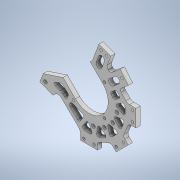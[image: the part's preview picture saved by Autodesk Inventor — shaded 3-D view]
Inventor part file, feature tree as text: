
AUTODESK INVENTOR PART (.ipt)
format: ipt  version: 2020 (Build 240168000, 168)  size: 1,079,296 bytes
history: native  units: mm
features: reference x29, sketch x22, extrude x18, projected_geometry x15, fillet x14, other x11, thicken_offset x5, hole x4, pattern_circular x3
ambient origin geometry x8: Origin, YZ Plane, XZ Plane, XY Plane, X Axis, Y Axis, Z Axis, Center Point
bodies: Solid1 (feature_tree)
feature tree (121):
  extrude  "Extrusion1"  Depth=45.0mm
  extrude  "Extrusion2"  Depth=5.0mm TaperAngle=0.0deg
  hole  "Hole1"  [1 undecoded]
  extrude  "Extrusion3"  Depth=10.0mm TaperAngle=0.0deg
  extrude  "Extrusion4"  Depth=10.0mm TaperAngle=0.0deg
  extrude  "Extrusion5"  Depth=3.0mm
  extrude  "Extrusion6"  Depth=3.0mm
  extrude  "Extrusion7"  Depth=3.0mm
  hole  "Hole2"  [1 undecoded]
  extrude  "Extrusion8"  Depth=7.0mm
  extrude  "Extrusion9"  Depth=10.0mm TaperAngle=0.0deg
  extrude  "Extrusion10"  Depth=10.0mm
  hole  "Hole3"  [1 undecoded]
  extrude  "Extrusion11"  Depth=10.0mm TaperAngle=0.0deg
  pattern_circular  "Circular Pattern1"  Count=6  [1 undecoded]
  pattern_circular  "Circular Pattern2"  Count=3  [1 undecoded]
  fillet  "Fillet3"  Radius=30.0mm
  pattern_circular  "Circular Pattern3"  Count=5  [1 undecoded]
  extrude  "Extrusion12"  Depth=2.0mm
  fillet  "Fillet5"  Radius=4.15mm
  extrude  "Extrusion14"  Depth=2.0mm
  extrude  "Extrusion15"  Depth=2.0mm
  thicken_offset  "Thicken1"
  fillet  "Fillet7"  Radius=10.0mm
  fillet  "Fillet8"  Radius=4.0mm
  extrude  "Extrusion16"  Depth=10.0mm TaperAngle=0.0deg
  hole  "Hole4"  [1 undecoded]
  fillet  "Fillet9"  Radius=1.0mm
  fillet  "Fillet10"  Radius=1.0mm
  fillet  "Fillet11"  Radius=5.0mm
  fillet  "Fillet12"  Radius=8.0mm
  extrude  "Extrusion17"  Depth=5.0mm TaperAngle=0.0deg
  fillet  "Fillet16"  Radius=6.0mm
  thicken_offset  "Thicken2"
  thicken_offset  "Thicken3"
  fillet  "Fillet17"  Radius=3.0mm
  fillet  "Fillet18"  Radius=4.0mm
  fillet  "Fillet19"  Radius=8.0mm
  fillet  "Fillet20"  Radius=5.0mm
  extrude  "Extrusion18"  Depth=2.0mm
  thicken_offset  "Thicken4"
  thicken_offset  "Thicken5"
  extrude  "Extrusion19"  Depth=2.0mm
  fillet  "Fillet21"  Radius=1.0mm
  sketch  "Sketch1"  dims[d0=109.0mm d1=45.0mm]
  reference  "Reference1"
  reference  "Reference2"
  reference  "Reference3"
  reference  "Reference4"
  sketch  "Sketch2"  dims[d2=106.0mm d3=5.0mm d4=0.0mm]
  reference  "Reference5"
  reference  "Reference6"
  reference  "Reference7"
  sketch  "Sketch3"  dims[d5=10.0mm d6=0.0mm]
  reference  "Reference8"
  reference  "Reference9"
  reference  "Reference10"
  reference  "Reference11"
  reference  "Reference12"
  reference  "Reference13"
  sketch  "Sketch4"  dims[d7=4.15mm d8=6.0mm d9=4.0mm d10=2.0mm d11=90.0deg d12=7.0mm d13=0.0mm d14=45.0mm]
  reference  "Reference14"
  sketch  "Sketch5"  dims[d15=10.0mm d16=0.0mm d17=10.0mm d18=0.0mm]
  projected_geometry  "Projected Loop1"
  reference  "Reference15"
  reference  "Reference16"
  reference  "Reference17"
  reference  "Reference18"
  sketch  "Sketch6"  dims[d19=10.0mm d20=0.0mm d21=10.0mm d22=0.0mm]
  projected_geometry  "Projected Loop2"
  sketch  "Sketch7"  dims[d24=3.0mm d25=3.0mm]
  projected_geometry  "Projected Loop3"
  sketch  "Sketch8"  dims[d26=3.0mm d27=3.0mm]
  sketch  "Sketch9"  dims[d28=3.0mm d29=3.0mm]
  projected_geometry  "Projected Loop4"
  reference  "Reference19"
  reference  "Reference20"
  sketch  "Sketch10"  dims[d30=10.0mm d31=0.0mm]
  projected_geometry  "Projected Loop5"
  sketch  "Sketch11"  dims[d32=3.0mm d33=6.0mm d34=4.0mm d35=2.0mm d36=90.0deg d37=7.0mm d38=0.0mm d39=7.0mm]
  projected_geometry  "Projected Loop6"
  sketch  "Sketch12"  dims[d40=7.0mm d41=7.0mm]
  projected_geometry  "Projected Loop7"
  sketch  "Sketch13"  dims[d42=7.0mm d43=10.0mm d44=0.0mm]
  reference  "Reference21"
  reference  "Reference22"
  reference  "Reference23"
  sketch  "Sketch14"  dims[d45=10.0mm d46=10.0mm]
  sketch  "Sketch15"  dims[d47=10.0mm d48=0.0mm d49=10.0mm]
  projected_geometry  "Projected Loop8"
  sketch  "Sketch17"  dims[d50=10.0mm d51=10.0mm d52=0.0mm]
  projected_geometry  "Projected Loop10"
  sketch  "Sketch18"  dims[d54=3.0mm d55=6.0mm d56=4.0mm d57=2.0mm d58=90.0deg d59=7.0mm d60=0.0mm d61=60.0mm]
  reference  "Reference24"
  reference  "Reference25"
  projected_geometry  "Projected Loop11"
  sketch  "Sketch19"  dims[d62=85.0mm]
  reference  "Reference26"
  projected_geometry  "Projected Loop12"
  sketch  "Sketch20"  dims[d63=30.0deg]
  projected_geometry  "Projected Loop13"
  reference  "Reference27"
  reference  "Reference28"
  reference  "Reference29"
  sketch  "Sketch21"  dims[d64=30.0deg]
  projected_geometry  "Projected Loop14"
  sketch  "Sketch22"  dims[d65=10.0mm d66=0.0mm d67=30.0mm d68=8.37758mm d70=30.0mm d71=8.37758mm]
  projected_geometry  "Projected Loop15"
  sketch  "Sketch23"  dims[d73=2.0mm d74=50.0mm d75=16.755161mm d77=4.15mm d78=4.15mm d79=4.15mm d80=4.15mm d81=10.0mm d82=0.0mm d89=4.0mm d91=10.0mm d92=0.0mm d93=5.0mm d94=0.0mm d95=1.0mm d96=1.0mm d97=5.0mm d98=8.0mm d99=5.0mm d100=0.0mm d101=3.0mm d102=6.0mm d103=4.0mm d104=2.0mm d105=90.0deg d106=17.0mm d107=0.0mm d108=6.0mm d109=3.0mm d110=4.0mm d111=8.0mm d112=5.0mm d113=0.0mm d117=2.0mm d118=1.0mm d119=1.0mm d120=1.0mm d121=1.0mm d122=2.0mm d123=10.0mm d124=2.0mm d125=2.0mm d126=12.0mm d127=12.0mm d128=4.0mm d129=8.0mm d130=4.0mm d131=8.0mm d132=5.0mm d133=0.0mm d134=0.5mm d135=0.5mm d136=0.5mm d137=0.5mm d138=5.0mm d139=0.0mm d140=2.0mm d114=0.5mm d115=0.872665mm]
  projected_geometry  "Projected Loop16"
  parser-record x2  (decoder bookkeeping rows leaked as tree rows — omitted from the tree; the rows remain in map.json)
  other  "reducer_1.iam"
  other  "xl_20:1"
  other  "motor_holder_2:1"
  other  "motor_holder_3:1"
  other  "xl_60:1"
  other  "motor_holder_1:1"
  other  "motor_holder_5:1"
  other  "slide_holder_1:1"
  other  "motor_holder_6:1"
note: 7 required parameter values undecoded (feature->parameter linkage not recoverable at this tier; creation-order binding heuristic only, values carry confidence <= 0.55)
note: 2 file-system paths scrubbed to <path> (originals preserved in map.json)
